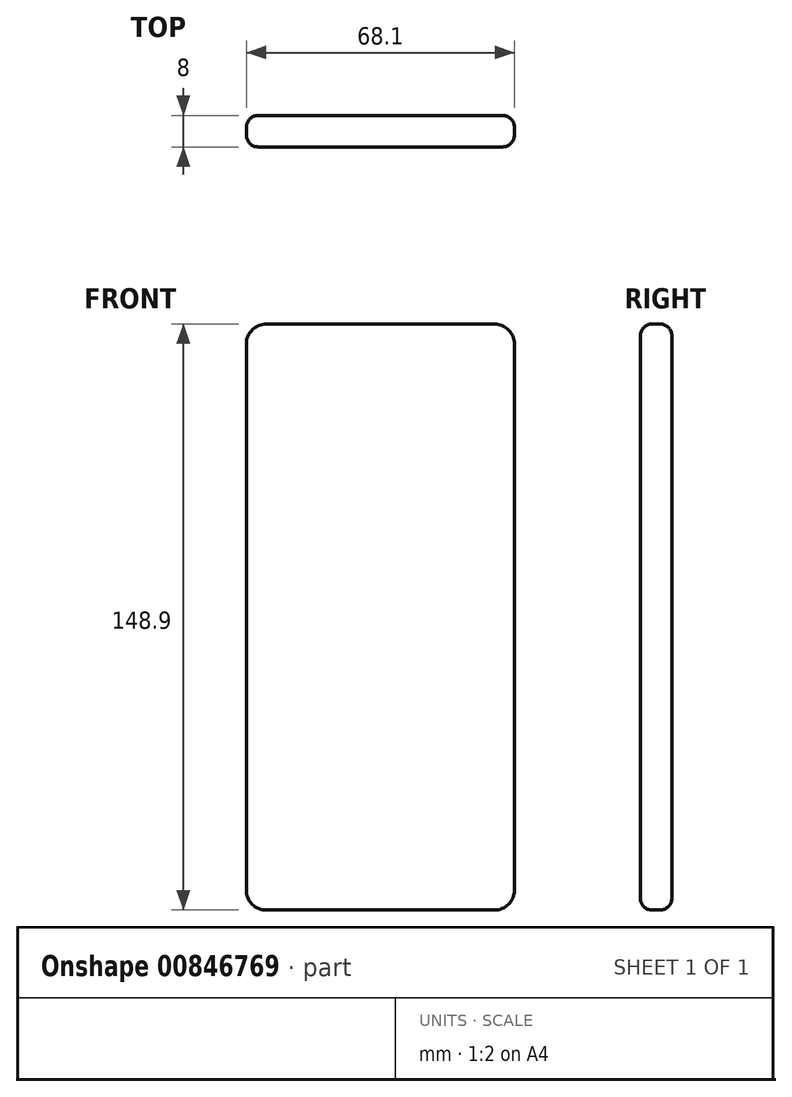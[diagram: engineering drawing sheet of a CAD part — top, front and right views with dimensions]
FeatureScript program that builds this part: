
annotation { "Feature Type Name" : "Feature", "Feature Type Description" : "" }
export const myFeature = defineFeature(function(context is Context, id is Id, definition is map)
    precondition{}
    {
        {
            var Q0;
            Q0=qCreatedBy(makeId("Front.planeOp"),FACE);
            var sketch = newSketch(context, id + "F0", { "sketchPlane" : qUnion([Q0])});
            skLineSegment(sketch, "E0.bottom", {"start": v(-26.48, 108.67) * mm, "end": v(41.62, 108.67) * mm});
            skLineSegment(sketch, "E0.top", {"start": v(-26.48, -40.23) * mm, "end": v(41.62, -40.23) * mm});
            skLineSegment(sketch, "E0.left", {"start": v(-26.48, 108.67) * mm, "end": v(-26.48, -40.23) * mm});
            skLineSegment(sketch, "E0.right", {"start": v(41.62, 108.67) * mm, "end": v(41.62, -40.23) * mm});
            skSolve(sketch);
        }
        {
            var Q0;
            Q0=makeQuery(id+"F0.imprint","IMPRINT",FACE,{"disambiguationData":[TD([[makeQuery(id+"F0.imprint","IMPRINT",EDGE,{"derivedFrom":sQuery(id+"F0.wireOp",EDGE,"E0.bottom")}),-1.0]])]});
            extrude(context, id + "F1", {"entities" : qUnion([Q0]), "depth" : 8 * mm, "offsetDistance" : 25.4 * mm});
        }
        {
            var Q0;
            Q0=makeQuery(id+"F1.opExtrude","CAP_FACE",FACE,{"disambiguationData":[OSD([sQuery(id+"F0.wireOp",EDGE,"E0.bottom"),sQuery(id+"F0.wireOp",EDGE,"E0.top"),sQuery(id+"F0.wireOp",EDGE,"E0.left"),sQuery(id+"F0.wireOp",EDGE,"E0.right")])],"isStart":false});
            fillet(context, id + "F2", {"entities" : qUnion([Q0]), "radius" : 3 * mm, "tangentPropagation" : true, "allowEdgeOverflow" : false});
        }
        {
            var Q0;
            Q0=makeQuery(id+"F1.opExtrude","CAP_FACE",FACE,{"disambiguationData":[OSD([sQuery(id+"F0.wireOp",EDGE,"E0.bottom"),sQuery(id+"F0.wireOp",EDGE,"E0.top"),sQuery(id+"F0.wireOp",EDGE,"E0.left"),sQuery(id+"F0.wireOp",EDGE,"E0.right")])],"isStart":true});
            fillet(context, id + "F3", {"entities" : qUnion([Q0]), "radius" : 3 * mm, "tangentPropagation" : true, "allowEdgeOverflow" : false});
        }
        {
            var Q0;
            Q0=makeQuery(id+"F2.opFillet","BLEND_EDGE",EDGE,{"blendedFrom":[makeQuery(id+"F1.opExtrude","CAP_EDGE",EDGE,{"disambiguationData":[OSD([sQuery(id+"F0.wireOp",EDGE,"E0.top")])],"isStart":false}),makeQuery(id+"F1.opExtrude","CAP_EDGE",EDGE,{"disambiguationData":[OSD([sQuery(id+"F0.wireOp",EDGE,"E0.right")])],"isStart":false})],"blendedInto":[]});
            fillet(context, id + "F4", {"entities" : qUnion([Q0]), "radius" : 5.08 * mm, "tangentPropagation" : true, "allowEdgeOverflow" : false});
        }
        {
            var Q0;
            Q0=makeQuery(id+"F1.opExtrude","SWEPT_EDGE",EDGE,{"disambiguationData":[OSD([sQuery(id+"F0.wireOp",EDGE,"E0.top"),sQuery(id+"F0.wireOp",EDGE,"E0.left")])]});
            var Q1;
            Q1=makeQuery(id+"F1.opExtrude","SWEPT_EDGE",EDGE,{"disambiguationData":[OSD([sQuery(id+"F0.wireOp",EDGE,"E0.bottom"),sQuery(id+"F0.wireOp",EDGE,"E0.left")])]});
            var Q2;
            Q2=makeQuery(id+"F1.opExtrude","SWEPT_EDGE",EDGE,{"disambiguationData":[OSD([sQuery(id+"F0.wireOp",EDGE,"E0.bottom"),sQuery(id+"F0.wireOp",EDGE,"E0.right")])]});
            fillet(context, id + "F5", {"entities" : qUnion([Q0, Q1, Q2]), "radius" : 5.08 * mm, "tangentPropagation" : true, "allowEdgeOverflow" : false});
        }
    });
